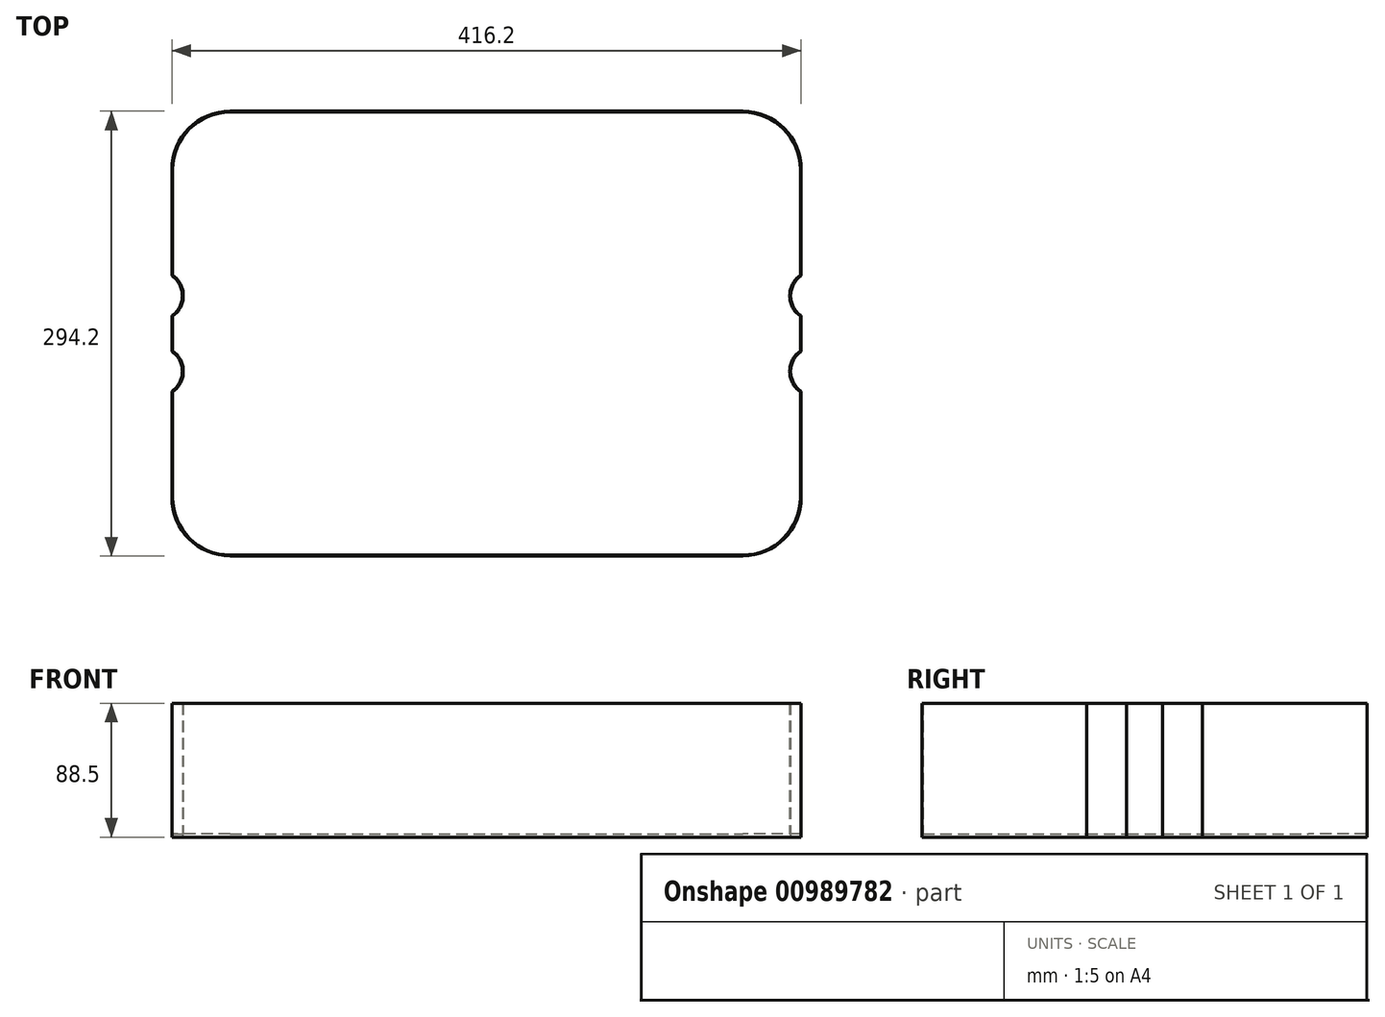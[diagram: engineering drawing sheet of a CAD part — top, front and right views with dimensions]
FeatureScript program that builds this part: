
annotation { "Feature Type Name" : "Feature", "Feature Type Description" : "" }
export const myFeature = defineFeature(function(context is Context, id is Id, definition is map)
    precondition{}
    {
        {
            var Q0;
            Q0=qCreatedBy(makeId("Top.planeOp"),FACE);
            var sketch = newSketch(context, id + "F0", { "sketchPlane" : qUnion([Q0])});
            skLineSegment(sketch, "E0.bottom", {"start": v(38, 0) * mm, "end": v(377, 0) * mm});
            skLineSegment(sketch, "E0.top", {"start": v(38, 293) * mm, "end": v(377, 293) * mm});
            skLineSegment(sketch, "E0.left", {"start": v(0, 38) * mm, "end": v(0, 108) * mm});
            skLineSegment(sketch, "E0.right", {"start": v(415, 38) * mm, "end": v(415, 108) * mm});
            skPoint(sketch, "E1.visualSharp", {"position": v(0, 293) * mm});
            skArc(sketch, "E1.filletArc", {"start": v(38, 293) * mm, "mid": v(11.13, 281.87) * mm, "end": v(0, 255) * mm});
            skPoint(sketch, "E2.visualSharp", {"position": v(415, 293) * mm});
            skArc(sketch, "E2.filletArc", {"start": v(415, 255) * mm, "mid": v(403.87, 281.87) * mm, "end": v(377, 293) * mm});
            skPoint(sketch, "E3.visualSharp", {"position": v(415, 0) * mm});
            skArc(sketch, "E3.filletArc", {"start": v(377, 0) * mm, "mid": v(403.87, 11.13) * mm, "end": v(415, 38) * mm});
            skPoint(sketch, "E4.visualSharp", {"position": v(0, 0) * mm});
            skArc(sketch, "E4.filletArc", {"start": v(0, 38) * mm, "mid": v(11.13, 11.13) * mm, "end": v(38, 0) * mm});
            skArc(sketch, "E5", {"start": v(0, 185) * mm, "mid": v(7, 171.5) * mm, "end": v(0, 158) * mm});
            skLineSegment(sketch, "E6", {"start": v(0, 146.5) * mm, "end": v(415, 146.5) * mm, "construction": true});
            skLineSegment(sketch, "E7", {"start": v(207.5, 293) * mm, "end": v(207.5, 0) * mm, "construction": true});
            skArc(sketch, "E8.MirrorCS", {"start": v(0, 108) * mm, "mid": v(7, 121.5) * mm, "end": v(0, 135) * mm});
            skArc(sketch, "E9.MirrorCS", {"start": v(415, 185) * mm, "mid": v(408, 171.5) * mm, "end": v(415, 158) * mm});
            skArc(sketch, "E10.MirrorCS", {"start": v(415, 108) * mm, "mid": v(408, 121.5) * mm, "end": v(415, 135) * mm});
            skLineSegment(sketch, "E11.trimOffspring", {"start": v(0, 135) * mm, "end": v(0, 158) * mm});
            skLineSegment(sketch, "E12.trimOffspring", {"start": v(0, 185) * mm, "end": v(0, 255) * mm});
            skLineSegment(sketch, "E13.trimOffspring", {"start": v(415, 185) * mm, "end": v(415, 255) * mm});
            skLineSegment(sketch, "E14.trimOffspring", {"start": v(415, 135) * mm, "end": v(415, 158) * mm});
            skArc(sketch, "E15.0", {"start": v(38, 293.6) * mm, "mid": v(10.7, 282.3) * mm, "end": v(-0.6, 255) * mm});
            skLineSegment(sketch, "E15.1", {"start": v(-0.6, 184.69) * mm, "end": v(-0.6, 255) * mm});
            skArc(sketch, "E15.2", {"start": v(-0.6, 184.69) * mm, "mid": v(6.4, 171.5) * mm, "end": v(-0.6, 158.31) * mm});
            skLineSegment(sketch, "E15.3", {"start": v(-0.6, 134.69) * mm, "end": v(-0.6, 158.31) * mm});
            skArc(sketch, "E15.4", {"start": v(-0.6, 108.31) * mm, "mid": v(6.4, 121.5) * mm, "end": v(-0.6, 134.69) * mm});
            skLineSegment(sketch, "E15.5", {"start": v(415.6, 134.69) * mm, "end": v(415.6, 158.31) * mm});
            skArc(sketch, "E15.6", {"start": v(415.6, 184.69) * mm, "mid": v(408.6, 171.5) * mm, "end": v(415.6, 158.31) * mm});
            skLineSegment(sketch, "E15.7", {"start": v(415.6, 184.69) * mm, "end": v(415.6, 255) * mm});
            skArc(sketch, "E15.8", {"start": v(415.6, 255) * mm, "mid": v(404.3, 282.3) * mm, "end": v(377, 293.6) * mm});
            skArc(sketch, "E15.9", {"start": v(415.6, 108.31) * mm, "mid": v(408.6, 121.5) * mm, "end": v(415.6, 134.69) * mm});
            skLineSegment(sketch, "E15.10", {"start": v(415.6, 38) * mm, "end": v(415.6, 108.31) * mm});
            skArc(sketch, "E15.11", {"start": v(377, -0.6) * mm, "mid": v(404.3, 10.7) * mm, "end": v(415.6, 38) * mm});
            skLineSegment(sketch, "E15.12", {"start": v(38, -0.6) * mm, "end": v(377, -0.6) * mm});
            skArc(sketch, "E15.13", {"start": v(-0.6, 38) * mm, "mid": v(10.7, 10.7) * mm, "end": v(38, -0.6) * mm});
            skLineSegment(sketch, "E15.14", {"start": v(38, 293.6) * mm, "end": v(377, 293.6) * mm});
            skLineSegment(sketch, "E15.15", {"start": v(-0.6, 38) * mm, "end": v(-0.6, 108.31) * mm});
            skSolve(sketch);
        }
        {
            var Q0;
            Q0=makeQuery(id+"F0.imprint","IMPRINT",FACE,{"disambiguationData":[TD([[makeQuery(id+"F0.imprint","IMPRINT",EDGE,{"derivedFrom":sQuery(id+"F0.wireOp",EDGE,"E0.bottom")}),-1.0]])]});
            extrude(context, id + "F1", {"entities" : qUnion([Q0]), "depth" : 86.5 * mm, "offsetDistance" : 25 * mm});
        }
        {
            var Q0;
            Q0=makeQuery(id+"F0.imprint","IMPRINT",FACE,{"disambiguationData":[TD([[makeQuery(id+"F0.imprint","IMPRINT",EDGE,{"derivedFrom":sQuery(id+"F0.wireOp",EDGE,"E0.bottom")}),1.0]])]});
            var Q1;
            Q1=makeQuery(id+"F0.imprint","IMPRINT",FACE,{"disambiguationData":[TD([[makeQuery(id+"F0.imprint","IMPRINT",EDGE,{"derivedFrom":sQuery(id+"F0.wireOp",EDGE,"E0.bottom")}),-1.0]])]});
            extrude(context, id + "F2", {"entities" : qUnion([Q0, Q1]), "operationType" : NewBodyOperationType.ADD, "oppositeDirection" : true, "depth" : 2 * mm, "offsetDistance" : 25 * mm});
        }
    });
